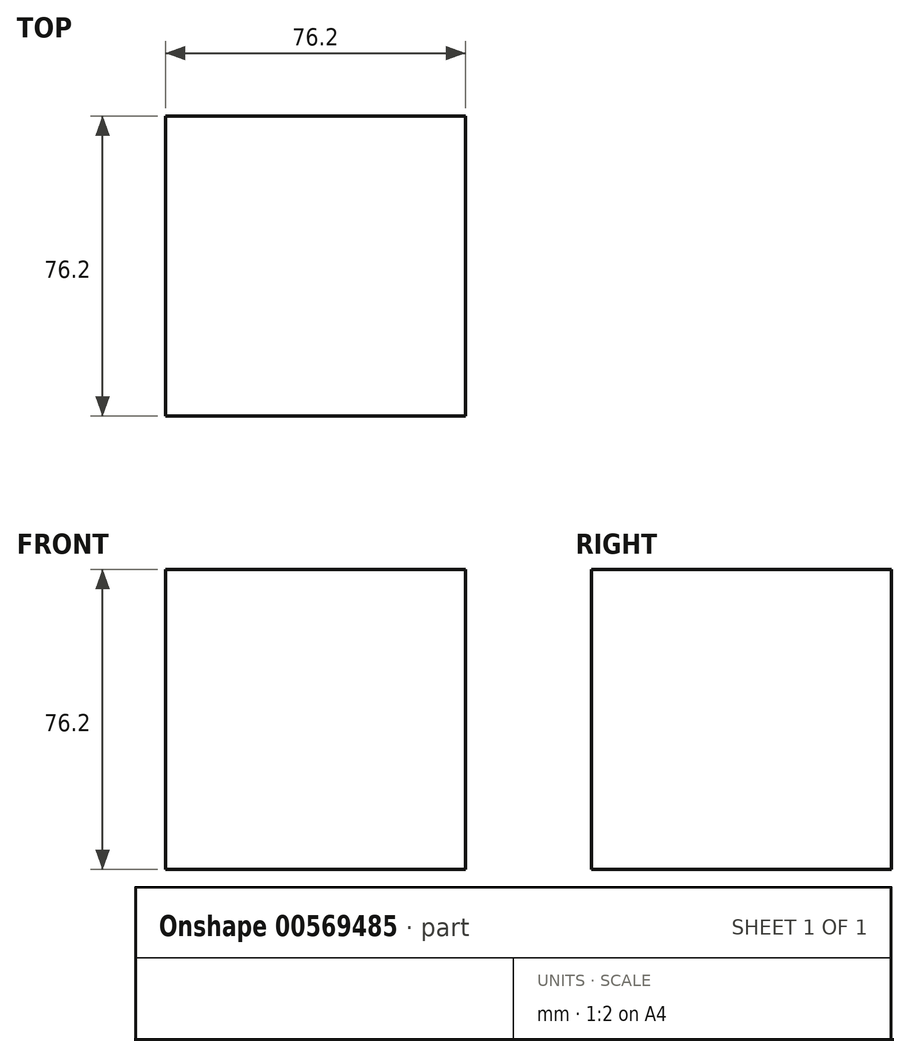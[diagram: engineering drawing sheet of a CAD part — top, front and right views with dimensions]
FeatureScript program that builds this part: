
annotation { "Feature Type Name" : "Feature", "Feature Type Description" : "" }
export const myFeature = defineFeature(function(context is Context, id is Id, definition is map)
    precondition{}
    {
        {
            var Q0;
            Q0=qCreatedBy(makeId("Front.planeOp"),FACE);
            var sketch = newSketch(context, id + "F0", { "sketchPlane" : qUnion([Q0])});
            skLineSegment(sketch, "E0.bottom", {"start": v(-31.27, 108.43) * mm, "end": v(44.93, 108.43) * mm});
            skLineSegment(sketch, "E0.top", {"start": v(-31.27, 32.23) * mm, "end": v(44.93, 32.23) * mm});
            skLineSegment(sketch, "E0.left", {"start": v(-31.27, 108.43) * mm, "end": v(-31.27, 32.23) * mm});
            skLineSegment(sketch, "E0.right", {"start": v(44.93, 108.43) * mm, "end": v(44.93, 32.23) * mm});
            skSolve(sketch);
        }
        {
            var Q0;
            Q0=makeQuery(id+"F0.imprint","IMPRINT",FACE,{"disambiguationData":[TD([[makeQuery(id+"F0.imprint","IMPRINT",EDGE,{"derivedFrom":sQuery(id+"F0.wireOp",EDGE,"E0.bottom")}),-1.0]])]});
            extrude(context, id + "F1", {"entities" : qUnion([Q0]), "depth" : 76.2 * mm, "offsetDistance" : 25.4 * mm});
        }
    });
